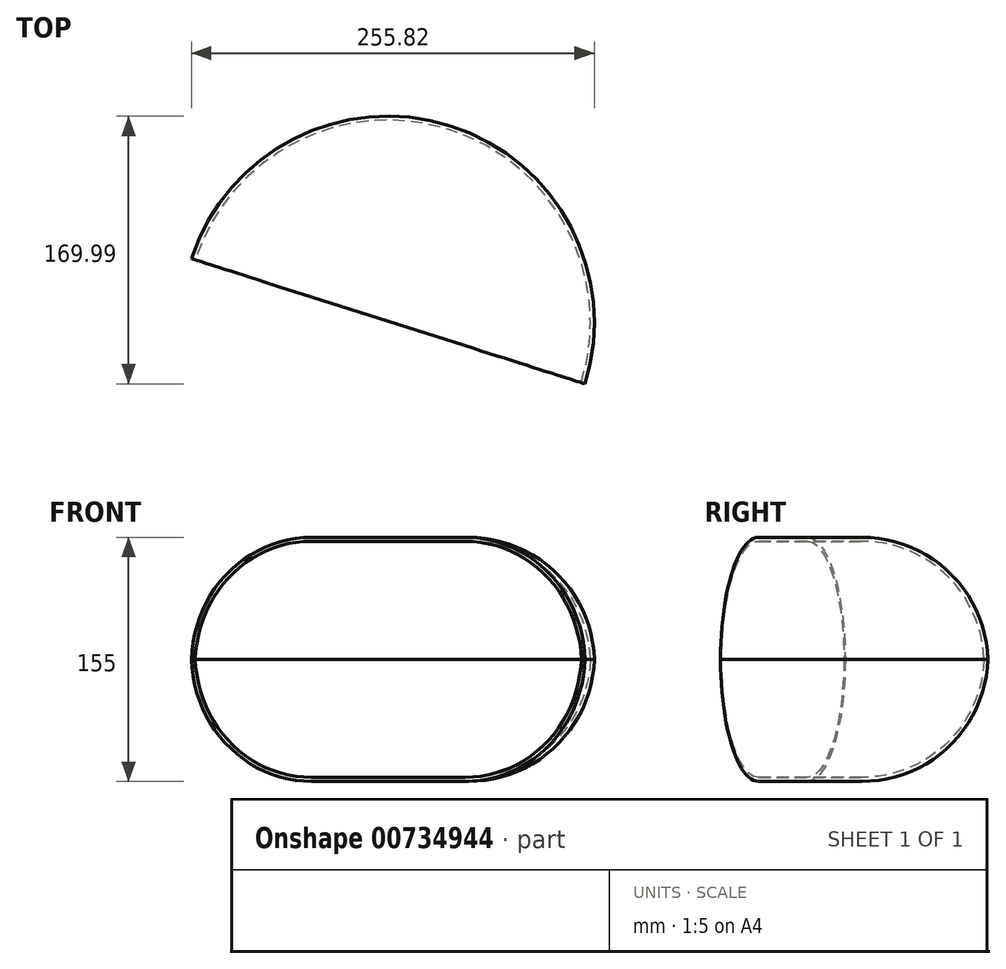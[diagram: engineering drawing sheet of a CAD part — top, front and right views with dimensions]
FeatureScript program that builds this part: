
annotation { "Feature Type Name" : "Feature", "Feature Type Description" : "" }
export const myFeature = defineFeature(function(context is Context, id is Id, definition is map)
    precondition{}
    {
        {
            var Q0;
            Q0=qCreatedBy(makeId("Top.planeOp"),FACE);
            var sketch = newSketch(context, id + "F0", { "sketchPlane" : qUnion([Q0])});
            skArc(sketch, "E0", {"start": v(88.83, -61.94) * mm, "mid": v(3.29, 101.93) * mm, "end": v(-161.17, 17.51) * mm});
            skLineSegment(sketch, "E1", {"start": v(-161.17, 17.51) * mm, "end": v(88.83, -61.94) * mm});
            skSolve(sketch);
        }
        {
            var Q0;
            Q0=makeQuery(id+"F0.imprint","IMPRINT",FACE,{"disambiguationData":[TD([[makeQuery(id+"F0.imprint","IMPRINT",EDGE,{"derivedFrom":sQuery(id+"F0.wireOp",EDGE,"E0")}),1.0]])]});
            extrude(context, id + "F1", {"entities" : qUnion([Q0]), "depth" : 155 * mm, "offsetDistance" : 25 * mm});
        }
        {
            var Q0;
            Q0=makeQuery(id+"F1.opExtrude","CAP_EDGE",EDGE,{"disambiguationData":[OSD([sQuery(id+"F0.wireOp",EDGE,"E0")])],"isStart":false});
            var Q1;
            Q1=makeQuery(id+"F1.opExtrude","CAP_EDGE",EDGE,{"disambiguationData":[OSD([sQuery(id+"F0.wireOp",EDGE,"E0")])],"isStart":true});
            fillet(context, id + "F2", {"entities" : qUnion([Q0, Q1]), "radius" : 80 * mm, "tangentPropagation" : true, "allowEdgeOverflow" : false});
        }
        {
            var Q0;
            Q0=makeQuery(id+"F1.opExtrude","SWEPT_FACE",FACE,{"disambiguationData":[OSD([sQuery(id+"F0.wireOp",EDGE,"E1")])]});
            shell(context, id + "F3", {"entities" : qUnion([Q0]), "thickness" : 2.5 * mm});
        }
    });
